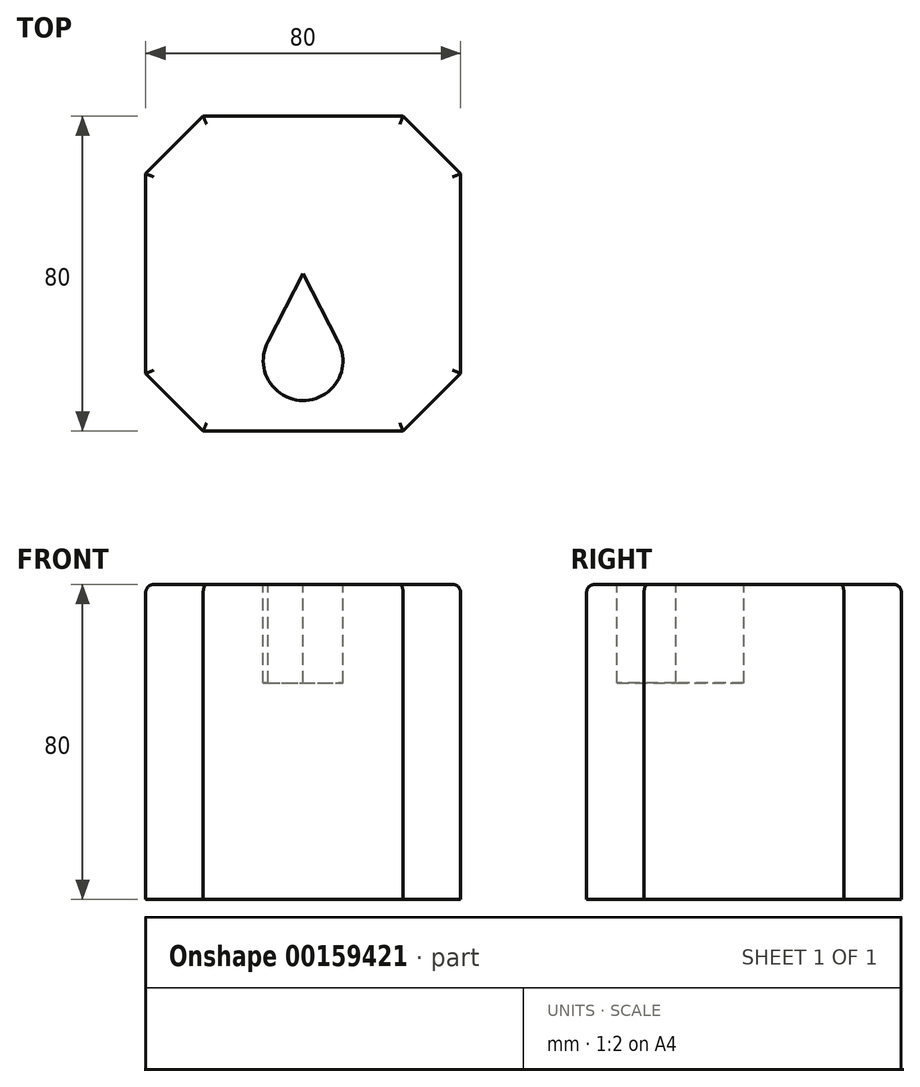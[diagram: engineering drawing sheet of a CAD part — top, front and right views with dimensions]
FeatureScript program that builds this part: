
annotation { "Feature Type Name" : "Feature", "Feature Type Description" : "" }
export const myFeature = defineFeature(function(context is Context, id is Id, definition is map)
    precondition{}
    {
        {
            var Q0;
            Q0=qCreatedBy(makeId("Top.planeOp"),FACE);
            var sketch = newSketch(context, id + "F0", { "sketchPlane" : qUnion([Q0])});
            skLineSegment(sketch, "E0", {"start": v(0, 40) * mm, "end": v(-25.4, 40) * mm});
            skLineSegment(sketch, "E1", {"start": v(-25.4, 40) * mm, "end": v(-40, 25.4) * mm});
            skLineSegment(sketch, "E2", {"start": v(-40, 25.4) * mm, "end": v(-40, 0) * mm});
            skLineSegment(sketch, "E3", {"start": v(0, 40) * mm, "end": v(0, 0) * mm, "construction": true});
            skLineSegment(sketch, "E4", {"start": v(0, 0) * mm, "end": v(-40, 0) * mm, "construction": true});
            skLineSegment(sketch, "E5.1.0", {"start": v(-25.4, -40) * mm, "end": v(0, -40) * mm});
            skLineSegment(sketch, "E5.1.1", {"start": v(-40, -25.4) * mm, "end": v(-25.4, -40) * mm});
            skLineSegment(sketch, "E5.1.2", {"start": v(-40, 0) * mm, "end": v(-40, -25.4) * mm});
            skLineSegment(sketch, "E5.2.0", {"start": v(40, -25.4) * mm, "end": v(40, 0) * mm});
            skLineSegment(sketch, "E5.2.1", {"start": v(25.4, -40) * mm, "end": v(40, -25.4) * mm});
            skLineSegment(sketch, "E5.2.2", {"start": v(0, -40) * mm, "end": v(25.4, -40) * mm});
            skLineSegment(sketch, "E5.3.0", {"start": v(25.4, 40) * mm, "end": v(0, 40) * mm});
            skLineSegment(sketch, "E5.3.1", {"start": v(40, 25.4) * mm, "end": v(25.4, 40) * mm});
            skLineSegment(sketch, "E5.3.2", {"start": v(40, 0) * mm, "end": v(40, 25.4) * mm});
            skPoint(sketch, "E5.center", {"position": v(0, 0) * mm});
            skSolve(sketch);
        }
        {
            var Q0;
            Q0=makeQuery(id+"F0.imprint","IMPRINT",FACE,{"disambiguationData":[TD([[makeQuery(id+"F0.imprint","IMPRINT",EDGE,{"derivedFrom":sQuery(id+"F0.wireOp",EDGE,"E0")}),1.0]])]});
            extrude(context, id + "F1", {"entities" : qUnion([Q0]), "depth" : 80 * mm});
        }
        {
            var Q0;
            Q0=makeQuery(id+"F1.opExtrude","CAP_FACE",FACE,{"disambiguationData":[OSD([sQuery(id+"F0.wireOp",EDGE,"E0"),sQuery(id+"F0.wireOp",EDGE,"E1"),sQuery(id+"F0.wireOp",EDGE,"E2"),sQuery(id+"F0.wireOp",EDGE,"E5.1.0"),sQuery(id+"F0.wireOp",EDGE,"E5.1.1"),sQuery(id+"F0.wireOp",EDGE,"E5.1.2"),sQuery(id+"F0.wireOp",EDGE,"E5.2.0"),sQuery(id+"F0.wireOp",EDGE,"E5.2.1"),sQuery(id+"F0.wireOp",EDGE,"E5.2.2"),sQuery(id+"F0.wireOp",EDGE,"E5.3.0"),sQuery(id+"F0.wireOp",EDGE,"E5.3.1"),sQuery(id+"F0.wireOp",EDGE,"E5.3.2")])],"isStart":false});
            fillet(context, id + "F2", {"entities" : qUnion([Q0]), "radius" : 2 * mm, "tangentPropagation" : true, "allowEdgeOverflow" : false});
        }
        {
            var Q0;
            Q0=makeQuery(id+"F1.opExtrude","CAP_FACE",FACE,{"disambiguationData":[OSD([sQuery(id+"F0.wireOp",EDGE,"E0"),sQuery(id+"F0.wireOp",EDGE,"E1"),sQuery(id+"F0.wireOp",EDGE,"E2"),sQuery(id+"F0.wireOp",EDGE,"E5.1.0"),sQuery(id+"F0.wireOp",EDGE,"E5.1.1"),sQuery(id+"F0.wireOp",EDGE,"E5.1.2"),sQuery(id+"F0.wireOp",EDGE,"E5.2.0"),sQuery(id+"F0.wireOp",EDGE,"E5.2.1"),sQuery(id+"F0.wireOp",EDGE,"E5.2.2"),sQuery(id+"F0.wireOp",EDGE,"E5.3.0"),sQuery(id+"F0.wireOp",EDGE,"E5.3.1"),sQuery(id+"F0.wireOp",EDGE,"E5.3.2")])],"isStart":false});
            var sketch = newSketch(context, id + "F3", { "sketchPlane" : qUnion([Q0])});
            skCircle(sketch, "E6", {"center": v(0, -22.12) * mm, "radius": 10.14 * mm});
            skLineSegment(sketch, "E7", {"start": v(0, 0) * mm, "end": v(0, -22.12) * mm, "construction": true});
            skLineSegment(sketch, "E8", {"start": v(-8.87, -17.23) * mm, "end": v(0, 0) * mm});
            skLineSegment(sketch, "E9", {"start": v(0, 0) * mm, "end": v(9, -17.48) * mm});
            skSolve(sketch);
        }
        {
            var Q0;
            {var subQ0=sQuery(id+"F3.wireOp",EDGE,"E8");Q0=makeQuery(id+"F3.imprint","IMPRINT",FACE,{"disambiguationData":[TD([[makeQuery(id+"F3.imprint","IMPRINT",EDGE,{"derivedFrom":subQ0}),-1.0]])]});}
            var Q1;
            {var subQ0=sQuery(id+"F3.wireOp",EDGE,"E6");var subQ1=makeQuery(id+"F3.imprint","INTERSECT",VERTEX,{"derivedFrom":[subQ0,sQuery(id+"F3.wireOp",EDGE,"E8")]});Q1=makeQuery(id+"F3.imprint","IMPRINT",FACE,{"disambiguationData":[TD([[makeQuery(id+"F3.imprint","IMPRINT",EDGE,{"disambiguationData":[TD([[subQ1,1.0]])],"derivedFrom":subQ0}),1.0]])]});}
            extrude(context, id + "F4", {"entities" : qUnion([Q0, Q1]), "operationType" : NewBodyOperationType.REMOVE, "oppositeDirection" : true, "depth" : 25 * mm});
        }
    });
